# Revit family: 3025685
name_source: partatom
category: Modelli generici
revit_build: Autodesk Revit 2018 (Build: 20170223_1515(x64)
units: mm (PartAtom-declared; Revit-internal decimal feet)

## family parameters
Basato su piano di lavoro = No
Condiviso = No
Punto di calcolo locali = No
Può ospitare armatura = No
Quota connettore circolare = Usa diametro
Sempre verticale = Sì
Taglio con vuoti quando caricato = No
Tipo di parte = Normale

## types (1)
- ARES 300 TEC ErP
     GAS connection diameter = 51 mm
    Boiler material = Boiler Material
    Boiler material1 = Boiler Material 1
    Diameter of fume exhaust = 200 mm  [stored 0.656168 ft]
    Dimensions of Piping Connectors = 51 mm
    Display Material = Boiler Display material
    Electric Power = 26 W
    Frequency of use = 50 Hz
    Hot water flow = 83.3 L/s
    Hydraulic Fittings = 2.5
    Manufacturer Product Link = https://www.immergas.com
    Mass = 386.00 kg
    MasterFormat = 23 00 00- Heating, Ventilating, and Air Conditioning (HVAC)
    Modello = ARES 300 TEC ErP
    Name BIM&CO = Caldaia
    Nominal Current = 435 A
    Nominal Voltage = 230 V
    Operating Temperature = 90 °C
    Overall Depth = 770 mm  [stored 2.52625 ft]
    Overall Height = 1150 mm
    Overall Width = 1300 mm  [stored 4.26509 ft]
    Piping volume boiler = 0.03 m³
    Product Code = 3.025685
    Produttore = Immergas
    Thermal flow rate = 300000
    Thermal power 80/60°C = 294000 W
    Uniformat = Heat Generating Systems
    Uniformat code = D3020
    yield hvac heating load nominal (%) = 98
    yield hvac heating load nominal 30 (%) = 96.2

note: source unit labels omitted for Thermal flow rate — the stored unit's dimension contradicts the parameter name (converter mislabeling)

note: [stored X ft] marks values corroborated as IEEE doubles in the binary element streams (Revit-internal decimal feet)
